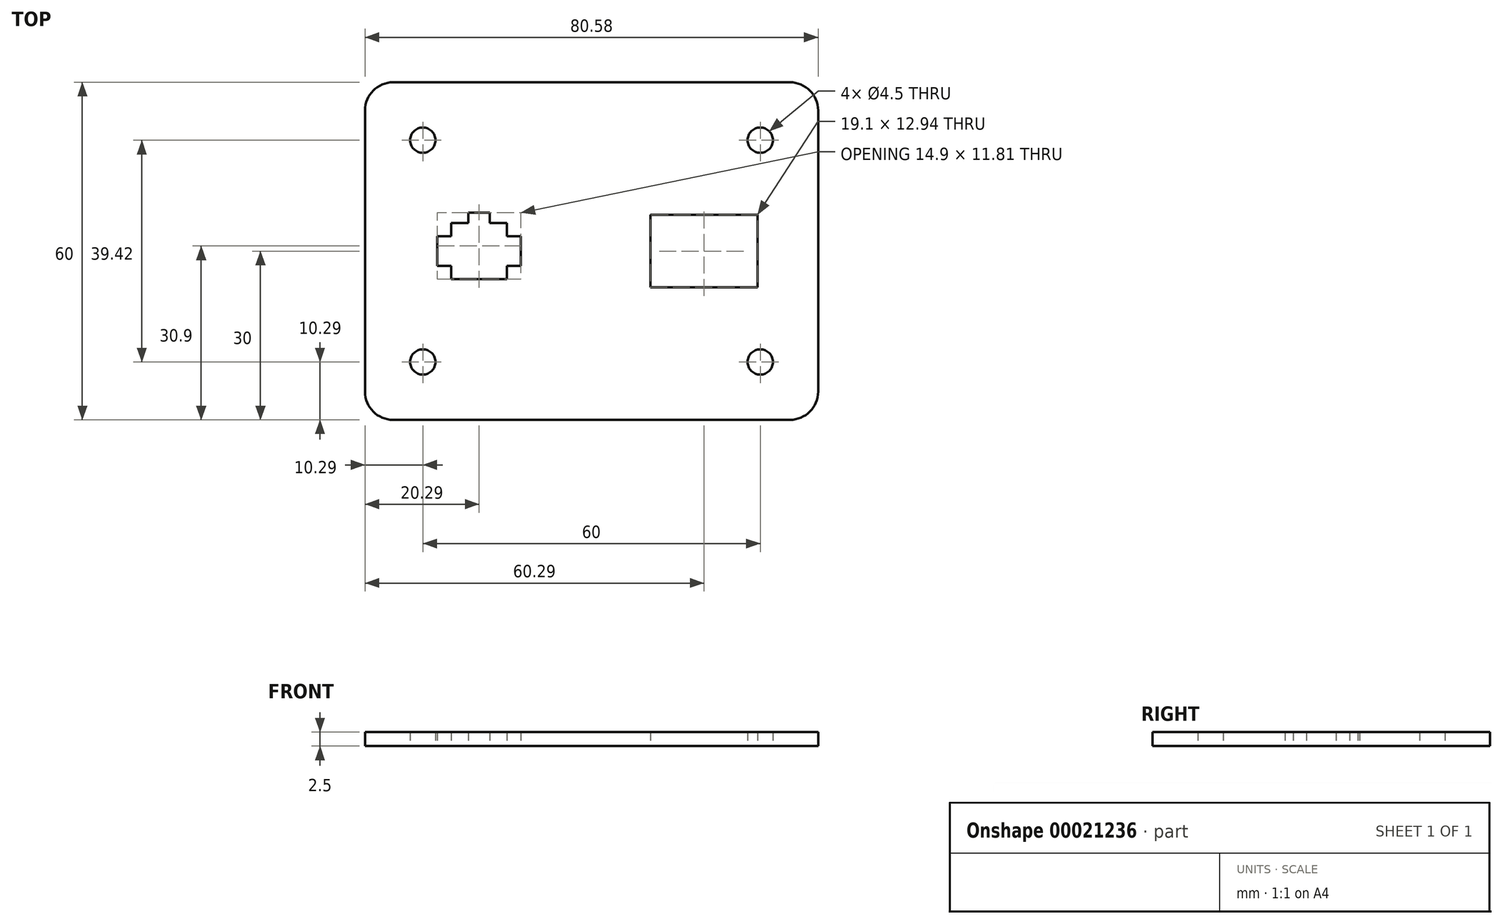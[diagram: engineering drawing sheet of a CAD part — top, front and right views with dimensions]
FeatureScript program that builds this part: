
annotation { "Feature Type Name" : "Feature", "Feature Type Description" : "" }
export const myFeature = defineFeature(function(context is Context, id is Id, definition is map)
    precondition{}
    {
        {
            var Q0;
            Q0=qCreatedBy(makeId("Top.planeOp"),FACE);
            var sketch = newSketch(context, id + "F0", { "sketchPlane" : qUnion([Q0])});
            skLineSegment(sketch, "E0.rect.bottom", {"start": v(35.3, -30) * mm, "end": v(-35.3, -30) * mm});
            skLineSegment(sketch, "E0.rect.top", {"start": v(35.29, 30) * mm, "end": v(-35.3, 30) * mm});
            skLineSegment(sketch, "E0.rect.left", {"start": v(40.3, -25) * mm, "end": v(40.3, 25) * mm});
            skLineSegment(sketch, "E0.rect.right", {"start": v(-40.3, -25) * mm, "end": v(-40.3, 25) * mm});
            skPoint(sketch, "E0.rect.middle", {"position": v(0, 0) * mm});
            skLineSegment(sketch, "E1", {"start": v(0, 30) * mm, "end": v(0, -30) * mm, "construction": true});
            skLineSegment(sketch, "E2", {"start": v(-40.29, 0) * mm, "end": v(40.29, 0) * mm, "construction": true});
            skCircle(sketch, "E3", {"center": v(-30, 19.7) * mm, "radius": 2.25 * mm});
            skCircle(sketch, "E4.MirrorC", {"center": v(30, 19.71) * mm, "radius": 2.25 * mm});
            skCircle(sketch, "E5.MirrorC", {"center": v(30, -19.71) * mm, "radius": 2.25 * mm});
            skCircle(sketch, "E6.MirrorC", {"center": v(-30, -19.71) * mm, "radius": 2.25 * mm});
            skLineSegment(sketch, "E7", {"start": v(-20, 30) * mm, "end": v(-20, -30) * mm, "construction": true});
            skLineSegment(sketch, "E8.MirrorCS", {"start": v(20, 30) * mm, "end": v(20, -30) * mm, "construction": true});
            skLineSegment(sketch, "E9", {"start": v(-20, -5) * mm, "end": v(-15.03, -5) * mm});
            skLineSegment(sketch, "E10", {"start": v(-15.02, 2.65) * mm, "end": v(-12.55, 2.65) * mm});
            skLineSegment(sketch, "E11", {"start": v(-12.55, -2.65) * mm, "end": v(-12.55, 2.65) * mm});
            skLineSegment(sketch, "E12", {"start": v(-12.55, -2.65) * mm, "end": v(-15.02, -2.65) * mm});
            skLineSegment(sketch, "E13", {"start": v(-21.93, 5) * mm, "end": v(-21.93, 6.8) * mm});
            skLineSegment(sketch, "E14", {"start": v(-20, 6.8) * mm, "end": v(-21.93, 6.8) * mm});
            skLineSegment(sketch, "E15.MirrorCS", {"start": v(-20, 6.8) * mm, "end": v(-18.08, 6.8) * mm});
            skLineSegment(sketch, "E16.MirrorCS", {"start": v(-18.08, 5) * mm, "end": v(-18.08, 6.8) * mm});
            skLineSegment(sketch, "E17.MirrorCS", {"start": v(-27.45, -2.65) * mm, "end": v(-24.98, -2.65) * mm});
            skLineSegment(sketch, "E18.MirrorCS", {"start": v(-27.45, -2.65) * mm, "end": v(-27.45, 2.65) * mm});
            skLineSegment(sketch, "E19.MirrorCS", {"start": v(-24.98, 2.65) * mm, "end": v(-27.45, 2.65) * mm});
            skLineSegment(sketch, "E20.MirrorCS", {"start": v(-20, -5) * mm, "end": v(-24.98, -5) * mm});
            skLineSegment(sketch, "E21", {"start": v(30, -19.71) * mm, "end": v(30, -30) * mm, "construction": true});
            skLineSegment(sketch, "E22", {"start": v(30, -19.71) * mm, "end": v(40.3, -19.71) * mm, "construction": true});
            skPoint(sketch, "E23.visualSharp", {"position": v(-40.29, 30) * mm});
            skArc(sketch, "E23.filletArc", {"start": v(-35.3, 30) * mm, "mid": v(-38.83, 28.54) * mm, "end": v(-40.3, 25) * mm});
            skPoint(sketch, "E24.visualSharp", {"position": v(40.3, 30) * mm});
            skArc(sketch, "E24.filletArc", {"start": v(40.3, 25) * mm, "mid": v(38.83, 28.54) * mm, "end": v(35.29, 30) * mm});
            skPoint(sketch, "E25.visualSharp", {"position": v(40.3, -30) * mm});
            skArc(sketch, "E25.filletArc", {"start": v(35.3, -30) * mm, "mid": v(38.83, -28.54) * mm, "end": v(40.29, -25) * mm});
            skPoint(sketch, "E26.visualSharp", {"position": v(-40.29, -30) * mm});
            skArc(sketch, "E26.filletArc", {"start": v(-40.29, -25) * mm, "mid": v(-38.83, -28.54) * mm, "end": v(-35.3, -30) * mm});
            skLineSegment(sketch, "E27", {"start": v(-24.98, 5) * mm, "end": v(-21.93, 5) * mm});
            skLineSegment(sketch, "E28", {"start": v(-18.08, 5) * mm, "end": v(-15.03, 5) * mm});
            skLineSegment(sketch, "E29", {"start": v(-24.98, 2.65) * mm, "end": v(-24.98, 5) * mm});
            skLineSegment(sketch, "E30", {"start": v(-24.98, -2.65) * mm, "end": v(-24.98, -5) * mm});
            skLineSegment(sketch, "E31", {"start": v(-15.03, -5) * mm, "end": v(-15.03, -2.65) * mm});
            skLineSegment(sketch, "E32", {"start": v(-15.03, 2.65) * mm, "end": v(-15.03, 5) * mm});
            skLineSegment(sketch, "E33.rect.bottom", {"start": v(29.55, -6.47) * mm, "end": v(10.45, -6.47) * mm});
            skLineSegment(sketch, "E33.rect.top", {"start": v(29.55, 6.47) * mm, "end": v(10.45, 6.47) * mm});
            skLineSegment(sketch, "E33.rect.left", {"start": v(29.55, -6.47) * mm, "end": v(29.55, 6.47) * mm});
            skLineSegment(sketch, "E33.rect.right", {"start": v(10.45, -6.47) * mm, "end": v(10.45, 6.47) * mm});
            skPoint(sketch, "E33.rect.middle", {"position": v(20, 0) * mm});
            skSolve(sketch);
        }
        {
            var Q0;
            Q0 = qSketchRegion(id + "F0", true);
            extrude(context, id + "F1", {"entities" : qUnion([Q0]), "depth" : 2.5 * mm});
        }
    });
